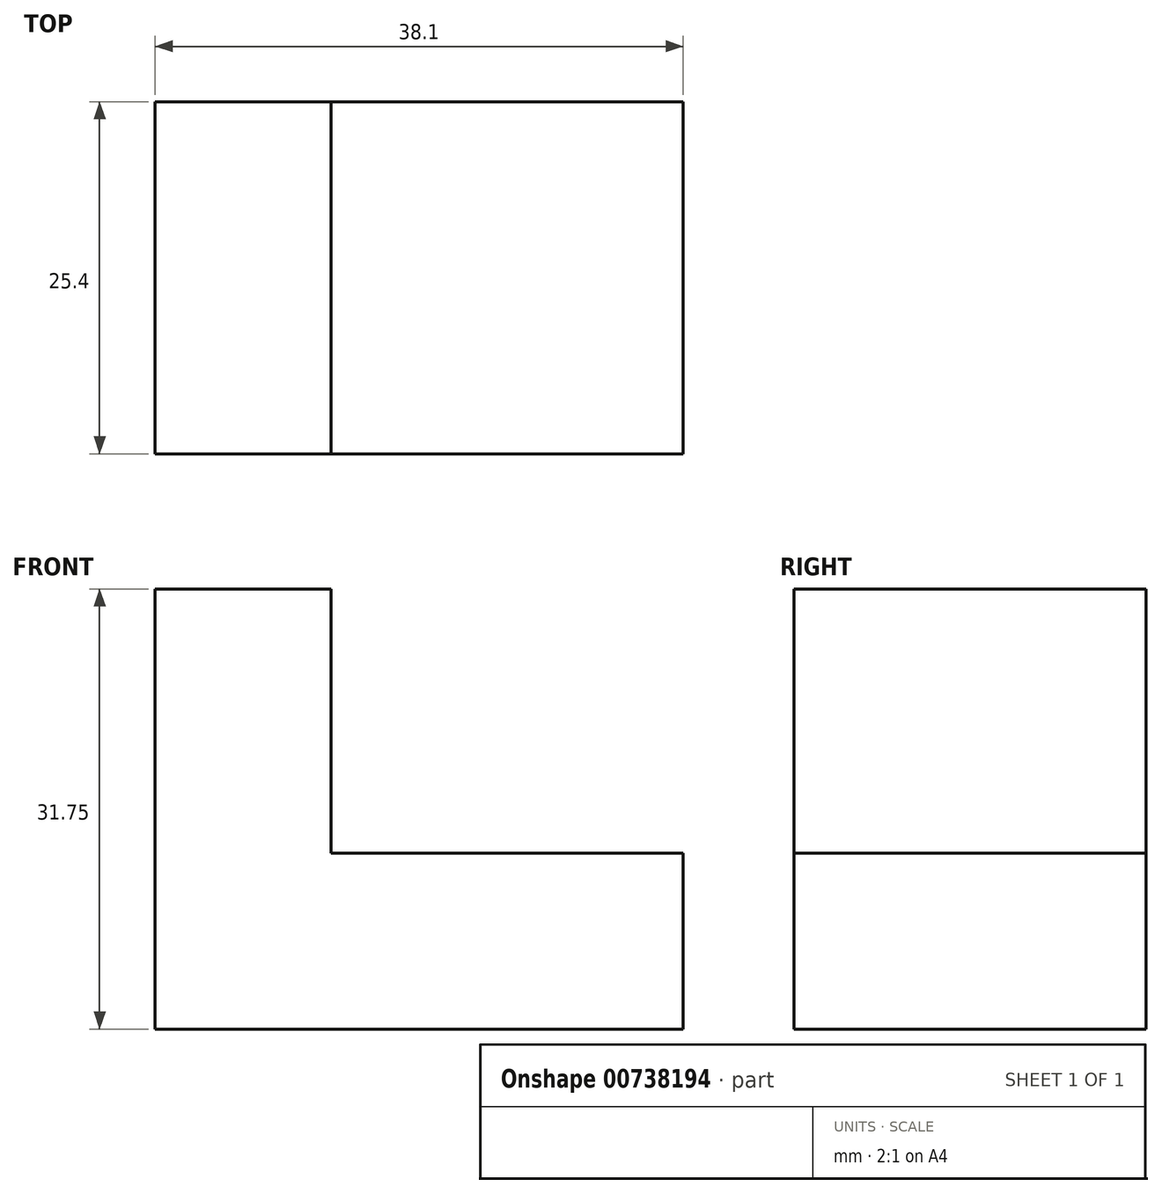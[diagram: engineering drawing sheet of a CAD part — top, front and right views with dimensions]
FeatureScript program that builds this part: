
annotation { "Feature Type Name" : "Feature", "Feature Type Description" : "" }
export const myFeature = defineFeature(function(context is Context, id is Id, definition is map)
    precondition{}
    {
        {
            var Q0;
            Q0=qCreatedBy(makeId("Front.planeOp"),FACE);
            var sketch = newSketch(context, id + "F0", { "sketchPlane" : qUnion([Q0])});
            skLineSegment(sketch, "E0", {"start": v(0, 31.75) * mm, "end": v(0, 0) * mm});
            skLineSegment(sketch, "E1", {"start": v(0, 0) * mm, "end": v(38.1, 0) * mm});
            skLineSegment(sketch, "E2", {"start": v(38.1, 0) * mm, "end": v(38.1, 12.7) * mm});
            skLineSegment(sketch, "E3", {"start": v(38.1, 12.7) * mm, "end": v(12.7, 12.7) * mm});
            skLineSegment(sketch, "E4", {"start": v(12.7, 12.7) * mm, "end": v(12.7, 31.75) * mm});
            skLineSegment(sketch, "E5", {"start": v(12.7, 31.75) * mm, "end": v(0, 31.75) * mm});
            skSolve(sketch);
        }
        {
            var Q0;
            Q0=makeQuery(id+"F0.imprint","IMPRINT",FACE,{"disambiguationData":[TD([[makeQuery(id+"F0.imprint","IMPRINT",EDGE,{"derivedFrom":sQuery(id+"F0.wireOp",EDGE,"E0")}),1.0]])]});
            extrude(context, id + "F1", {"entities" : qUnion([Q0]), "depth" : 25.4 * mm, "offsetDistance" : 25.4 * mm});
        }
    });
